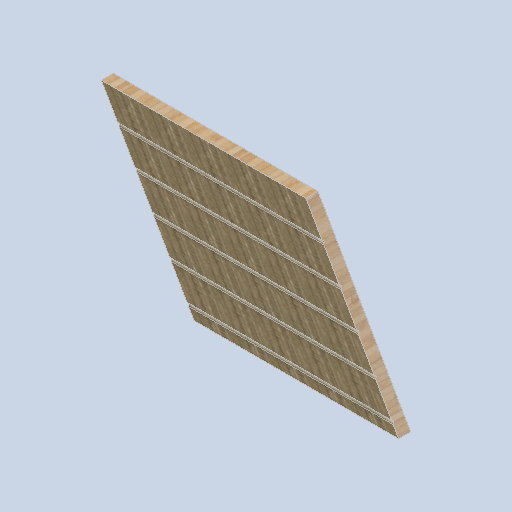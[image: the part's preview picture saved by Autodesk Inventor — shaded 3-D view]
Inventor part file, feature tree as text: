
AUTODESK INVENTOR PART (.ipt)
format: ipt  version: 2024.2 (Build 282272000, 272)  size: 420,864 bytes
history: native  units: mm
features: extrude x2, sketch x2, fillet x1
ambient origin geometry x8: Origin, YZ Plane, XZ Plane, XY Plane, X Axis, Y Axis, Z Axis, Center Point
bodies: Solid1 (feature_tree)
feature tree (5):
  extrude  "Extrusion1"  Depth=1696.0mm
  extrude  "Extrusion2"  Depth=10.0mm
  fillet  "Fillet1"  Radius=20.0mm
  sketch  "Sketch1"  dims[d0=1696.0mm d1=0.0mm d2=400.0mm]
  sketch  "Sketch2"  dims[d3=10.0mm d4=19.198622mm d5=20.0mm d6=19.198622mm d7=400.0mm d8=10.0mm d9=20.0mm d10=400.0mm d11=20.0mm d12=400.0mm d13=20.0mm d14=400.0mm d15=20.0mm d16=1696.0mm d17=0.0mm d18=10.0mm]
